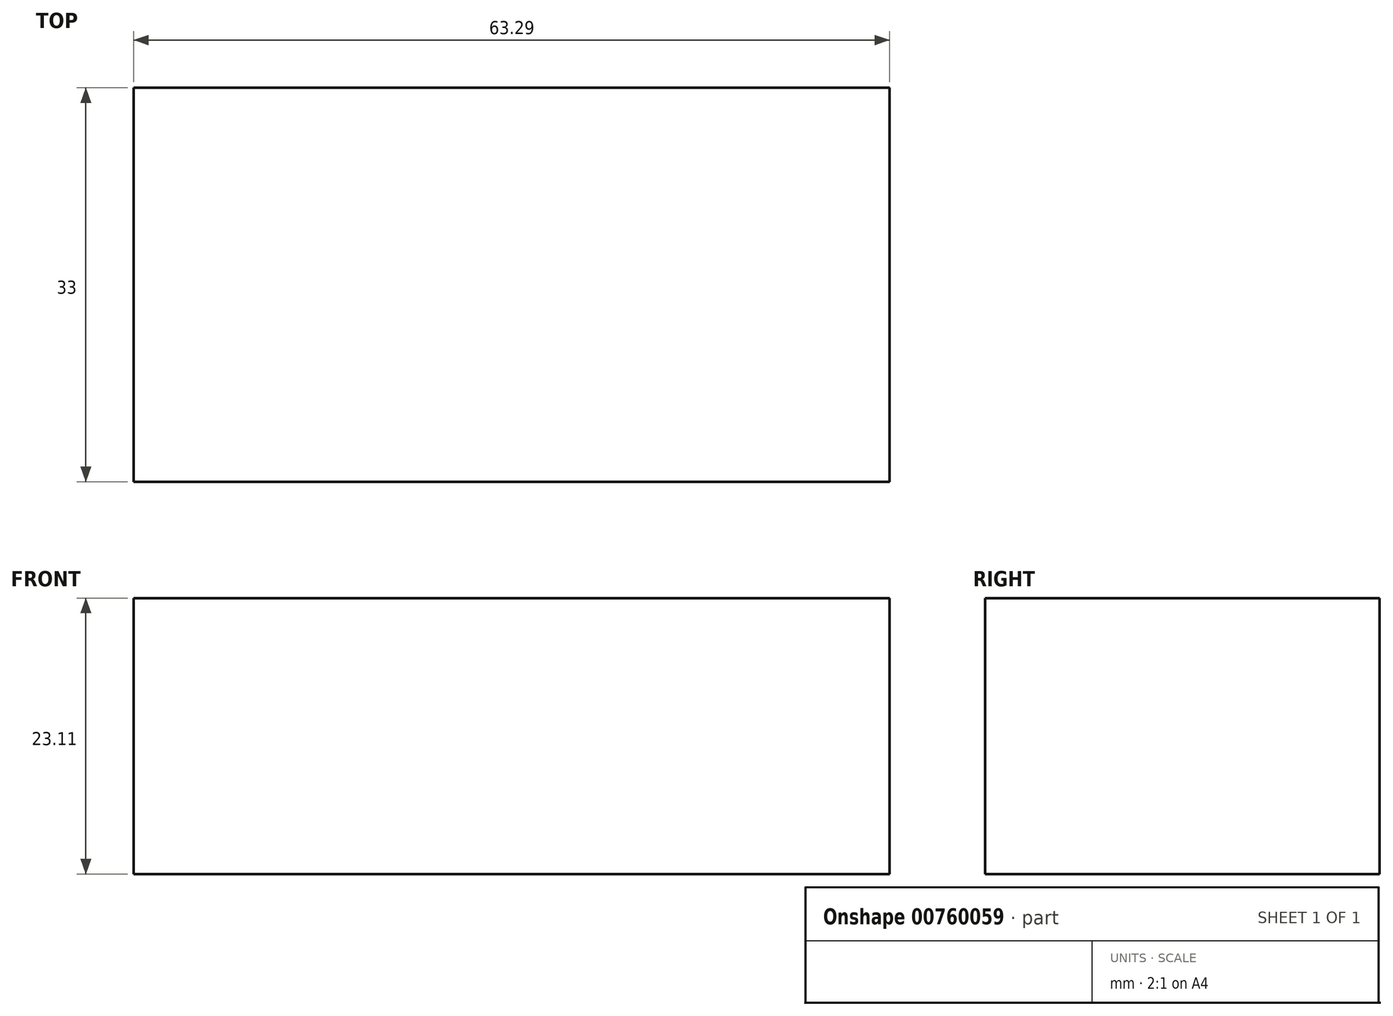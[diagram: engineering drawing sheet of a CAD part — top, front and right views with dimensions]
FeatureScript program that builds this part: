
annotation { "Feature Type Name" : "Feature", "Feature Type Description" : "" }
export const myFeature = defineFeature(function(context is Context, id is Id, definition is map)
    precondition{}
    {
        {
            var Q0;
            Q0=qCreatedBy(makeId("Top.planeOp"),FACE);
            var sketch = newSketch(context, id + "F0", { "sketchPlane" : qUnion([Q0])});
            skLineSegment(sketch, "E0.bottom", {"start": v(0, 0) * mm, "end": v(63.3, 0) * mm});
            skLineSegment(sketch, "E0.top", {"start": v(0, 33) * mm, "end": v(63.3, 33) * mm});
            skLineSegment(sketch, "E0.left", {"start": v(0, 0) * mm, "end": v(0, 33) * mm});
            skLineSegment(sketch, "E0.right", {"start": v(63.3, 0) * mm, "end": v(63.3, 33) * mm});
            skLineSegment(sketch, "E1", {"start": v(63.3, 33) * mm, "end": v(63.3, 57.26) * mm});
            skArc(sketch, "E2", {"start": v(63.3, 57.26) * mm, "mid": v(78.9, 72.87) * mm, "end": v(94.51, 57.26) * mm});
            skLineSegment(sketch, "E3.bottom", {"start": v(94.51, 57.26) * mm, "end": v(142.76, 57.26) * mm});
            skLineSegment(sketch, "E3.top", {"start": v(94.51, 33.33) * mm, "end": v(142.76, 33.33) * mm});
            skLineSegment(sketch, "E3.left", {"start": v(94.51, 57.26) * mm, "end": v(94.51, 33.33) * mm});
            skLineSegment(sketch, "E3.right", {"start": v(142.76, 57.26) * mm, "end": v(142.76, 33.33) * mm});
            skSolve(sketch);
        }
        {
            var Q0;
            Q0=makeQuery(id+"F0.imprint","IMPRINT",FACE,{"disambiguationData":[TD([[makeQuery(id+"F0.imprint","IMPRINT",EDGE,{"derivedFrom":sQuery(id+"F0.wireOp",EDGE,"E0.bottom")}),1.0]])]});
            extrude(context, id + "F1", {"entities" : qUnion([Q0]), "depth" : 23.1 * mm, "offsetDistance" : 25.4 * mm});
        }
    });
